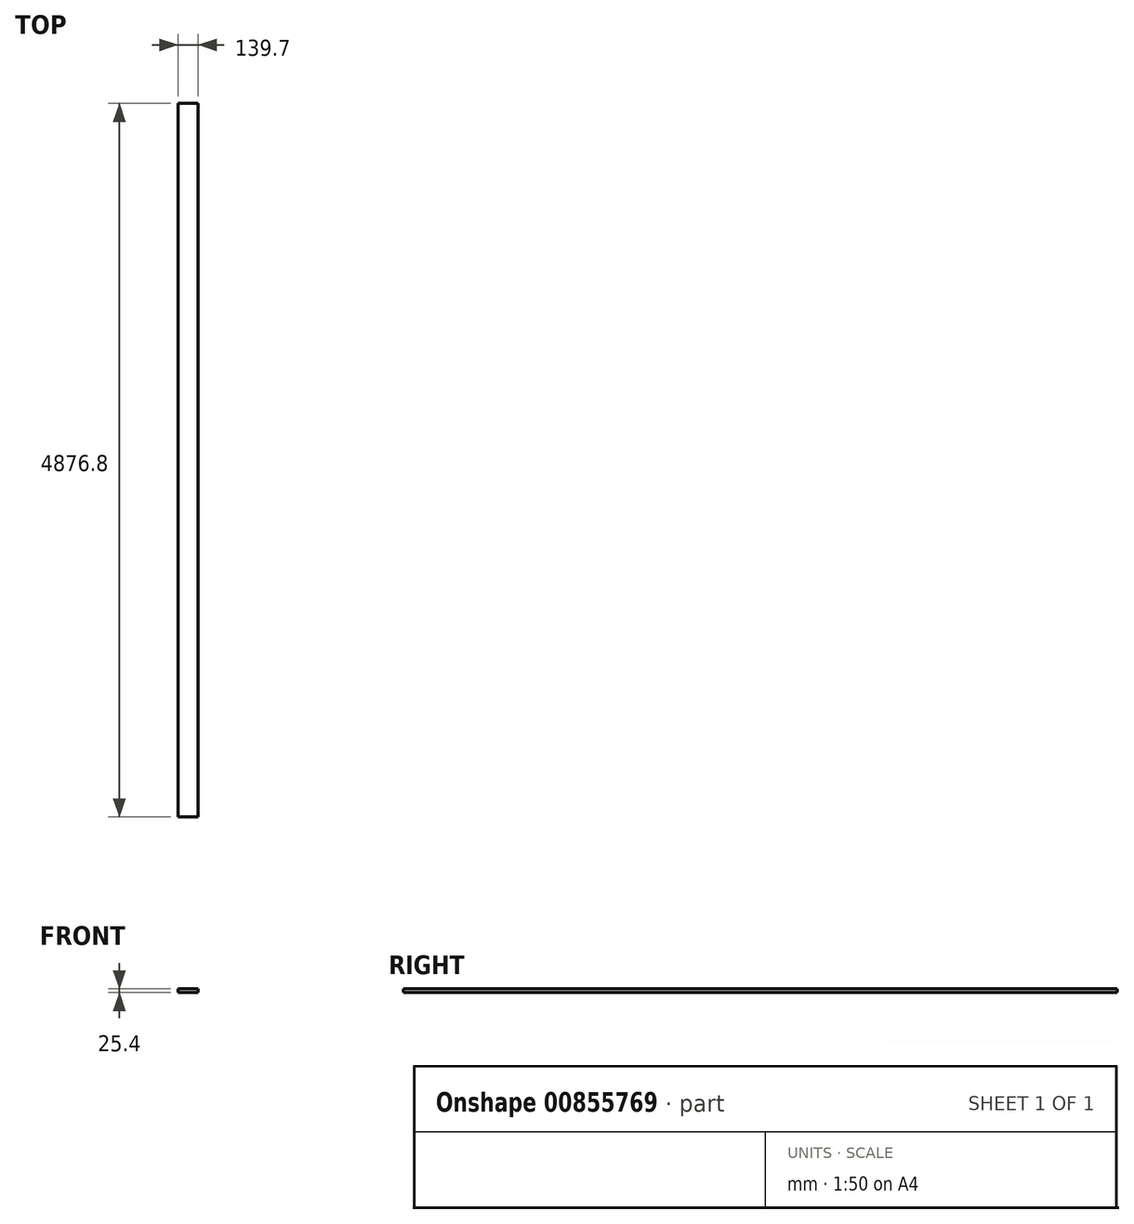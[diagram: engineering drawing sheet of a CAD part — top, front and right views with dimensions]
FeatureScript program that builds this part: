
annotation { "Feature Type Name" : "Feature", "Feature Type Description" : "" }
export const myFeature = defineFeature(function(context is Context, id is Id, definition is map)
    precondition{}
    {
        {
            var Q0;
            Q0=qCreatedBy(makeId("Front.planeOp"),FACE);
            var sketch = newSketch(context, id + "F0", { "sketchPlane" : qUnion([Q0])});
            skLineSegment(sketch, "E0.bottom", {"start": v(0, 0) * mm, "end": v(139.7, 0) * mm});
            skLineSegment(sketch, "E0.top", {"start": v(0, 25.4) * mm, "end": v(139.7, 25.4) * mm});
            skLineSegment(sketch, "E0.left", {"start": v(0, 0) * mm, "end": v(0, 25.4) * mm});
            skLineSegment(sketch, "E0.right", {"start": v(139.7, 0) * mm, "end": v(139.7, 25.4) * mm});
            skSolve(sketch);
        }
        {
            var Q0;
            Q0=makeQuery(id+"F0.imprint","IMPRINT",FACE,{"disambiguationData":[TD([[makeQuery(id+"F0.imprint","IMPRINT",EDGE,{"derivedFrom":sQuery(id+"F0.wireOp",EDGE,"E0.bottom")}),1.0]])]});
            extrude(context, id + "F1", {"entities" : qUnion([Q0]), "oppositeDirection" : true, "depth" : 4876.8 * mm, "offsetDistance" : 25.4 * mm});
        }
    });
